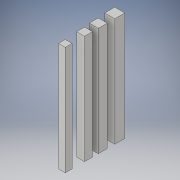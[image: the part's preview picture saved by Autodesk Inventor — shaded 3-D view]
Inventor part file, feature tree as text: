
AUTODESK INVENTOR PART (.ipt)
format: ipt  version: 2018 (Build 220112000, 112)  size: 110,592 bytes
history: native  units: in
note: dims shown in document units (in); Inventor stores cm internally (conversion verified against a paired STEP export)
features: extrude x1, sketch x1
ambient origin geometry x8: Origin, YZ Plane, XZ Plane, XY Plane, X Axis, Y Axis, Z Axis, Center Point
bodies: Solid1 (feature_tree)
feature tree (2):
  extrude  "Extrusion1"  Depth=0.145in
  sketch  "Sketch1"  dims[d0=0.125in d1=0.145in d2=0.165in d3=0.185in d5=2.0in d6=0.0in]
